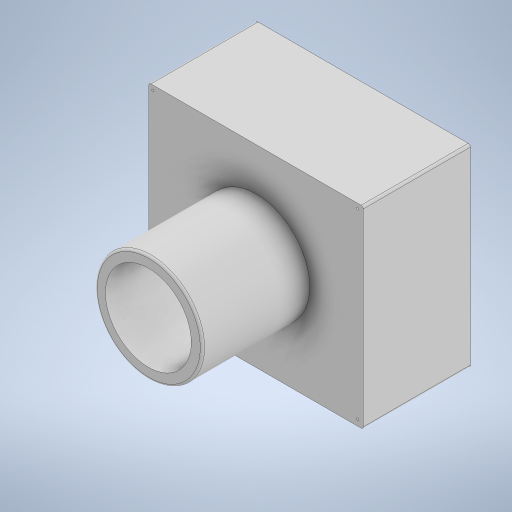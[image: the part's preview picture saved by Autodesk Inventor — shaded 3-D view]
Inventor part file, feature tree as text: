
AUTODESK INVENTOR PART (.ipt)
format: ipt  version: 2024 (Build 280153000, 153)  size: 266,752 bytes
history: native  units: mm
features: extrude x6, sketch x4, other x1, hole x1, fillet x1
ambient origin geometry x8: Origin, YZ Plane, XZ Plane, XY Plane, X Axis, Y Axis, Z Axis, Center Point
bodies: Body1 (feature_tree)
feature tree (13):
  other  "Sólido1"
  sketch  "Boceto1"  dims[d0=100.0mm d1=90.0mm]
  extrude  "Extrusión1"  Depth=90.0mm
  extrude  "Extrusión2"  Depth=50.0mm
  extrude  "Extrusión3"  Depth=50.0mm TaperAngle=0.0deg
  sketch  "Boceto3"  dims[d2=50.0mm d3=446.0mm]
  extrude  "Extrusión4"  Depth=50.0mm TaperAngle=0.0deg
  extrude  "Extrusión5"  Depth=50.0mm TaperAngle=0.0deg
  extrude  "Extrusión6"  Depth=50.0mm TaperAngle=0.0deg
  hole  "Agujero2"  [1 undecoded]
  fillet  "Empalme1"  Radius=1.0mm
  sketch  "Boceto5"  dims[d8=50.0mm d9=0.0mm d10=50.0mm d11=0.0mm d23=50.0mm d24=0.0mm d25=50.0mm d26=0.0mm d27=50.0mm d28=0.0mm d29=40.0mm d30=6.0mm d31=4.0mm d32=2.0mm d33=90.0deg d34=30.0mm d35=0.0mm d36=1.0mm d12=1.0mm d13=1.0mm d14=1.0mm d15=0.15mm d16=0.25mm d17=0.375mm d18=14.3117mm d19=0.75mm d20=20.594885mm d21=0.0625mm d22=0.75mm d37=20.594885mm d38=0.0625mm d39=0.75mm d40=0.375mm]
  sketch  "Boceto4"  dims[d5=1.0mm d6=50.0mm d7=0.0mm]
note: 1 required parameter value undecoded (feature->parameter linkage not recoverable at this tier; creation-order binding heuristic only, values carry confidence <= 0.55)
